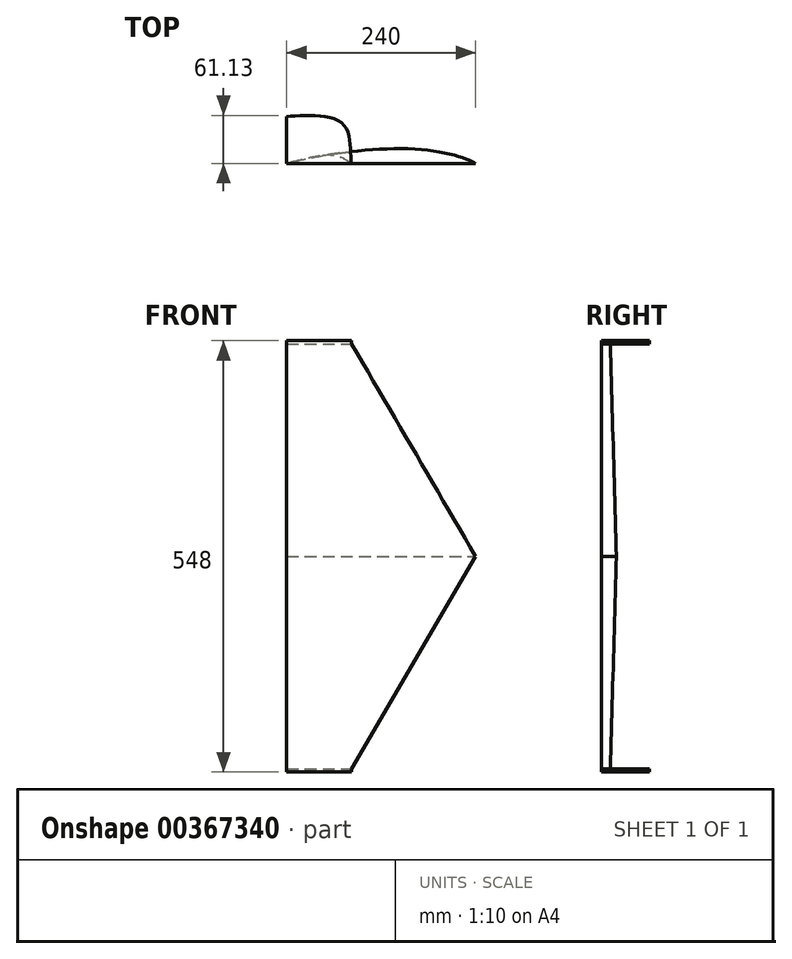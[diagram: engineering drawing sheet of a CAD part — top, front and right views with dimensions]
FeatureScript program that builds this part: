
annotation { "Feature Type Name" : "Feature", "Feature Type Description" : "" }
export const myFeature = defineFeature(function(context is Context, id is Id, definition is map)
    precondition{}
    {
        {
            assignVariable(context, id + "F0", {"name" : "wingspan", "anyValue" : 600 * mm});
        }
        {
            assignVariable(context, id + "F1", {"name" : "hullWidth", "anyValue" : 60});
        }
        {
            var Q0;
            Q0=qCreatedBy(makeId("Top.planeOp"),FACE);
            var sketch = newSketch(context, id + "F2", { "sketchPlane" : qUnion([Q0])});
            skFitSpline(sketch, "E0", {"points": [v(-42.19, 0) * mm, v(17.02, 10.8) * mm, v(40.47, 0) * mm], "startDerivative": vector(109.7, 31.5) * mm, "endDerivative": vector(51.58, -36.21) * mm});
            skLineSegment(sketch, "E1", {"start": v(-42.19, 0) * mm, "end": v(40.47, 0) * mm});
            skSolve(sketch);
        }
        {
            var Q0;
            Q0=makeQuery(id+"F2.imprint","IMPRINT",FACE,{"disambiguationData":[TD([[makeQuery(id+"F2.imprint","IMPRINT",EDGE,{"derivedFrom":sQuery(id+"F2.wireOp",EDGE,"E0")}),-1.0]])]});
            cPlane(context, id + "F3", {"entities" : qUnion([Q0]), "cplaneType" : CPlaneType.OFFSET, "offset" : (getVariable(context, 'wingspan') / 2) - (getVariable(context, 'hullWidth') / 2) * mm, "width" : 150 * mm, "height" : 150 * mm});
        }
        {
            var Q0;
            Q0=qCreatedBy(id+"F3.planeOp",FACE);
            var sketch = newSketch(context, id + "F4", { "sketchPlane" : qUnion([Q0])});
            skFitSpline(sketch, "E2", {"points": [v(-42.19, 0) * mm, v(111.62, 18.8) * mm, v(197.81, 0) * mm], "startDerivative": vector(111.73, 35.72) * mm, "endDerivative": vector(60.19, -46.2) * mm});
            skLineSegment(sketch, "E3", {"start": v(-42.19, 0) * mm, "end": v(197.81, 0) * mm});
            skSolve(sketch);
        }
        {
            var Q0;
            Q0=makeQuery(id+"F2.imprint","IMPRINT",FACE,{"disambiguationData":[TD([[makeQuery(id+"F2.imprint","IMPRINT",EDGE,{"derivedFrom":sQuery(id+"F2.wireOp",EDGE,"E0")}),-1.0]])]});
            var Q1;
            Q1=makeQuery(id+"F4.imprint","IMPRINT",FACE,{"disambiguationData":[TD([[makeQuery(id+"F4.imprint","IMPRINT",EDGE,{"derivedFrom":sQuery(id+"F4.wireOp",EDGE,"E2")}),-1.0]])]});
            loft(context, id + "F5", {"sheetProfilesArray" : [{ "sheetProfileEntities" : qUnion([Q0]) }, { "sheetProfileEntities" : qUnion([Q1]) }]});
        }
        {
            var Q0;
            Q0=makeQuery(id+"F5.opLoft","CAP_FACE",FACE,{"disambiguationData":[OSD([makeQuery(id+"F2.imprint","IMPRINT",FACE,{"disambiguationData":[TD([[makeQuery(id+"F2.imprint","IMPRINT",EDGE,{"derivedFrom":sQuery(id+"F2.wireOp",EDGE,"E0")}),-1.0]])]})])],"isStart":true});
            var sketch = newSketch(context, id + "F6", { "sketchPlane" : qUnion([Q0])});
            skFitSpline(sketch, "E4", {"points": [v(40.47, 0) * mm, v(29.2, -50.48) * mm, v(-42.19, -60) * mm], "startDerivative": vector(-16.9, -91.7) * mm, "endDerivative": vector(-109.6, 5.52) * mm});
            skLineSegment(sketch, "E5", {"start": v(-42.19, 0) * mm, "end": v(-42.19, -60) * mm});
            skLineSegment(sketch, "E6", {"start": v(40.47, 0) * mm, "end": v(-42.19, 0) * mm});
            skSolve(sketch);
        }
        {
            var Q0;
            Q0 = qSketchRegion(id + "F6", true);
            extrude(context, id + "F7", {"entities" : qUnion([Q0]), "operationType" : NewBodyOperationType.ADD, "depth" : 4 * mm});
        }
        {
            var Q0;
            Q0=makeQuery(id+"F5.opLoft","SWEPT_BODY",BODY,{"disambiguationData":[OSD([makeQuery(id+"F2.imprint","IMPRINT",FACE,{"disambiguationData":[TD([[makeQuery(id+"F2.imprint","IMPRINT",EDGE,{"derivedFrom":sQuery(id+"F2.wireOp",EDGE,"E0")}),-1.0]])]}),makeQuery(id+"F4.imprint","IMPRINT",FACE,{"disambiguationData":[TD([[makeQuery(id+"F4.imprint","IMPRINT",EDGE,{"derivedFrom":sQuery(id+"F4.wireOp",EDGE,"E2")}),-1.0]])]})])]});
            var Q1;
            Q1=makeQuery(id+"F5.opLoft","CAP_FACE",FACE,{"disambiguationData":[OSD([makeQuery(id+"F4.imprint","IMPRINT",FACE,{"disambiguationData":[TD([[makeQuery(id+"F4.imprint","IMPRINT",EDGE,{"derivedFrom":sQuery(id+"F4.wireOp",EDGE,"E2")}),-1.0]])]})])],"isStart":true});
            mirror(context, id + "F8", {"operationType" : NewBodyOperationType.ADD, "entities" : qUnion([Q0]), "mirrorPlane" : qUnion([Q1])});
        }
    });
